# Revit family: 531_OX_nofin
name_source: partatom
category: Windows
revit_build: Autodesk Revit 2016 (Build: 20150220_1215(x64)
units: mm (PartAtom-declared; Revit-internal decimal feet)

## family parameters
Always vertical = Yes
Cut with Voids When Loaded = No
Host = Wall
OmniClass Number = 23.30.20.00
OmniClass Title = Windows
Room Calculation Point = No
Shared = No

## types (87) — shared parameters
Default Sill Height = 31 1/2"
Wall Closure = By host

## per-type parameters (varying)
| type | Bar Set | Height | MLW | MLW2 | Width |
| 36x24 | 18" | 24" | 2 1/4" | 9" | 36" |
| 60x48 | 30" | 48" | 3 3/4" | 15" | 60" |
| 24x12Min | 12" | 12" | 1 1/2" | 6" | 24" |
| 72x36 | 36" | 60" | 4 1/2" | 18" | 72" |
| 96x60Max | 36" | 60" | 7 1/2" | 18" | 96" |
| 48x36 | 24" | 36" | 3" | 12" | 48" |
| 84x48 | 36" | 48" | 6" | 18" | 84" |
| 24x18 | 12" | 18" | 1 1/2" | 6" | 24" |
| 24x24 | 12" | 24" | 1 1/2" | 6" | 24" |
| 24x30 | 12" | 30" | 1 1/2" | 6" | 24" |
| 24x36 | 12" | 36" | 1 1/2" | 6" | 24" |
| 24x42 | 12" | 42" | 1 1/2" | 6" | 24" |
| 30x12 | 12" | 12" | 2 1/4" | 6" | 30" |
| 30x18 | 12" | 18" | 2 1/4" | 6" | 30" |
| 30x24 | 12" | 24" | 2 1/4" | 6" | 30" |
| 30x30 | 12" | 30" | 2 1/4" | 6" | 30" |
| 30x36 | 12" | 36" | 2 1/4" | 6" | 30" |
| 30x42 | 12" | 42" | 2 1/4" | 6" | 30" |
| 30x48 | 12" | 48" | 2 1/4" | 6" | 30" |
| 30x54 | 12" | 54" | 2 1/4" | 6" | 30" |
| 30x60 | 12" | 60" | 2 1/4" | 6" | 30" |
| 36x12 | 18" | 12" | 2 1/4" | 9" | 36" |
| 36x18 | 18" | 18" | 2 1/4" | 9" | 36" |
| 36x30 | 18" | 30" | 2 1/4" | 9" | 36" |
| 36x36 | 18" | 36" | 2 1/4" | 9" | 36" |
| 36x42 | 18" | 42" | 2 1/4" | 9" | 36" |
| 36x48 | 18" | 48" | 2 1/4" | 9" | 36" |
| 36x54 | 18" | 54" | 2 1/4" | 9" | 36" |
| 36x60 | 18" | 60" | 2 1/4" | 9" | 36" |
| 42x12 | 18" | 12" | 3" | 9" | 42" |
| 42x18 | 18" | 18" | 3" | 9" | 42" |
| 42x24 | 18" | 24" | 3" | 9" | 42" |
| 42x30 | 18" | 30" | 3" | 9" | 42" |
| 42x36 | 18" | 36" | 3" | 9" | 42" |
| 42x42 | 18" | 42" | 3" | 9" | 42" |
| 42x48 | 18" | 48" | 3" | 9" | 42" |
| 42x54 | 18" | 54" | 3" | 9" | 42" |
| 42x60 | 18" | 60" | 3" | 9" | 42" |
| 48x12 | 24" | 12" | 3" | 12" | 48" |
| 48x18 | 24" | 18" | 3" | 12" | 48" |
| 48x24 | 24" | 24" | 3" | 12" | 48" |
| 48x30 | 24" | 30" | 3" | 12" | 48" |
| 48x42 | 24" | 42" | 3" | 12" | 48" |
| 48x48 | 24" | 48" | 3" | 12" | 48" |
| 48x54 | 24" | 54" | 3" | 12" | 48" |
| 48x60 | 24" | 60" | 3" | 12" | 48" |
| 54x18 | 24" | 18" | 3 3/4" | 12" | 54" |
| 54x24 | 24" | 24" | 3 3/4" | 12" | 54" |
| 54x30 | 24" | 30" | 3 3/4" | 12" | 54" |
| 54x36 | 24" | 36" | 3 3/4" | 12" | 54" |
| 54x42 | 24" | 42" | 3 3/4" | 12" | 54" |
| 54x48 | 24" | 48" | 3 3/4" | 12" | 54" |
| 54x54 | 24" | 54" | 3 3/4" | 12" | 54" |
| 54x60 | 24" | 60" | 3 3/4" | 12" | 54" |
| 60x24 | 30" | 24" | 3 3/4" | 15" | 60" |
| 60x30 | 30" | 30" | 3 3/4" | 15" | 60" |
| 60x36 | 30" | 36" | 3 3/4" | 15" | 60" |
| 60x42 | 30" | 42" | 3 3/4" | 15" | 60" |
| 60x54 | 30" | 54" | 3 3/4" | 15" | 60" |
| 60x60 | 30" | 60" | 3 3/4" | 15" | 60" |
| 66x36 | 30" | 36" | 4 1/2" | 15" | 66" |
| 66x42 | 30" | 42" | 4 1/2" | 15" | 66" |
| 66x48 | 30" | 48" | 4 1/2" | 15" | 66" |
| 66x54 | 30" | 54" | 4 1/2" | 15" | 66" |
| 66x60 | 30" | 60" | 4 1/2" | 15" | 66" |
| 72x42 | 36" | 42" | 4 1/2" | 18" | 72" |
| 72x48 | 36" | 48" | 4 1/2" | 18" | 72" |
| 72x54 | 36" | 54" | 4 1/2" | 18" | 72" |
| 72x60 | 36" | 60" | 4 1/2" | 18" | 72" |
| 78x36 | 36" | 36" | 5 1/4" | 18" | 78" |
| 78x42 | 36" | 42" | 5 1/4" | 18" | 78" |
| 78x48 | 36" | 48" | 5 1/4" | 18" | 78" |
| 78x54 | 36" | 54" | 5 1/4" | 18" | 78" |
| 78x60 | 36" | 60" | 5 1/4" | 18" | 78" |
| 84x36 | 36" | 36" | 6" | 18" | 84" |
| 84x42 | 36" | 42" | 6" | 18" | 84" |
| 84x54 | 36" | 54" | 6" | 18" | 84" |
| 84x60 | 36" | 60" | 6" | 18" | 84" |
| 90x36 | 36" | 36" | 6 3/4" | 18" | 90" |
| 90x42 | 36" | 42" | 6 3/4" | 18" | 90" |
| 90x48 | 36" | 48" | 6 3/4" | 18" | 90" |
| 90x54 | 36" | 54" | 6 3/4" | 18" | 90" |
| 90x60 | 36" | 60" | 6 3/4" | 18" | 90" |
| 96x36 | 36" | 36" | 7 1/2" | 18" | 96" |
| 96x42 | 36" | 42" | 7 1/2" | 18" | 96" |
| 96x48 | 36" | 48" | 7 1/2" | 18" | 96" |
| 96x54 | 36" | 54" | 7 1/2" | 18" | 96" |

## geometry (parser evidence)
native form markers: Sweep x3
no freeform markers — native parametric forms only
